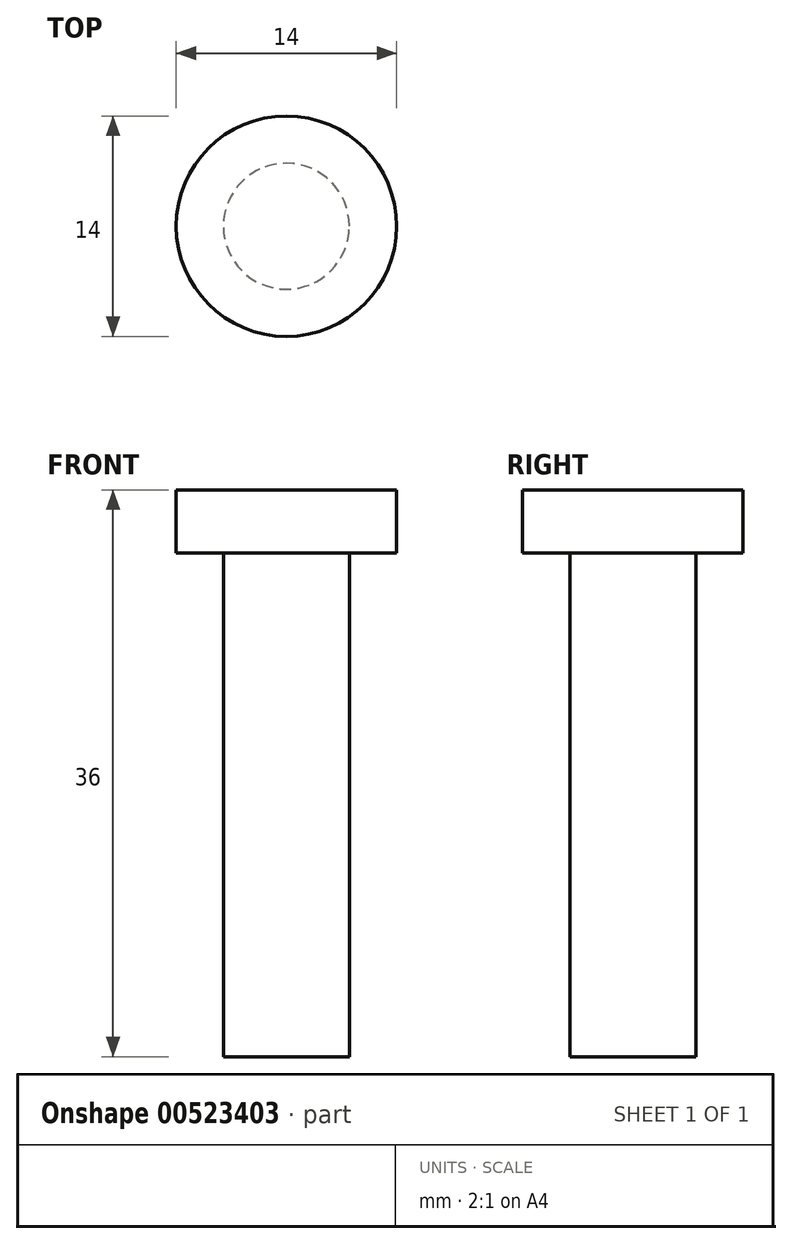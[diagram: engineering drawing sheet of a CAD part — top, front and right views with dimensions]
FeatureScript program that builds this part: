
annotation { "Feature Type Name" : "Feature", "Feature Type Description" : "" }
export const myFeature = defineFeature(function(context is Context, id is Id, definition is map)
    precondition{}
    {
        {
            var Q0;
            Q0=qCreatedBy(makeId("Front.planeOp"),FACE);
            var sketch = newSketch(context, id + "F0", { "sketchPlane" : qUnion([Q0])});
            skLineSegment(sketch, "E0", {"start": v(0, 0) * mm, "end": v(-4, 0) * mm});
            skLineSegment(sketch, "E1", {"start": v(-4, 0) * mm, "end": v(-4, 32) * mm});
            skLineSegment(sketch, "E2", {"start": v(-4, 32) * mm, "end": v(-7, 32) * mm});
            skLineSegment(sketch, "E3", {"start": v(-7, 32) * mm, "end": v(-7, 36) * mm});
            skLineSegment(sketch, "E4", {"start": v(-7, 36) * mm, "end": v(0, 36) * mm});
            skLineSegment(sketch, "E5", {"start": v(0, 36) * mm, "end": v(0, 0) * mm});
            skSolve(sketch);
        }
        {
            var Q0;
            Q0 = qSketchRegion(id + "F0", true);
            var Q1;
            Q1=sQuery(id+"F0.wireOp",EDGE,"E5");
            revolve(context, id + "F1", {"surfaceOperationType" : NewSurfaceOperationType.NEW, "entities" : qUnion([Q0]), "axis" : qUnion([Q1]), "revolveType" : RevolveType.FULL});
        }
    });
